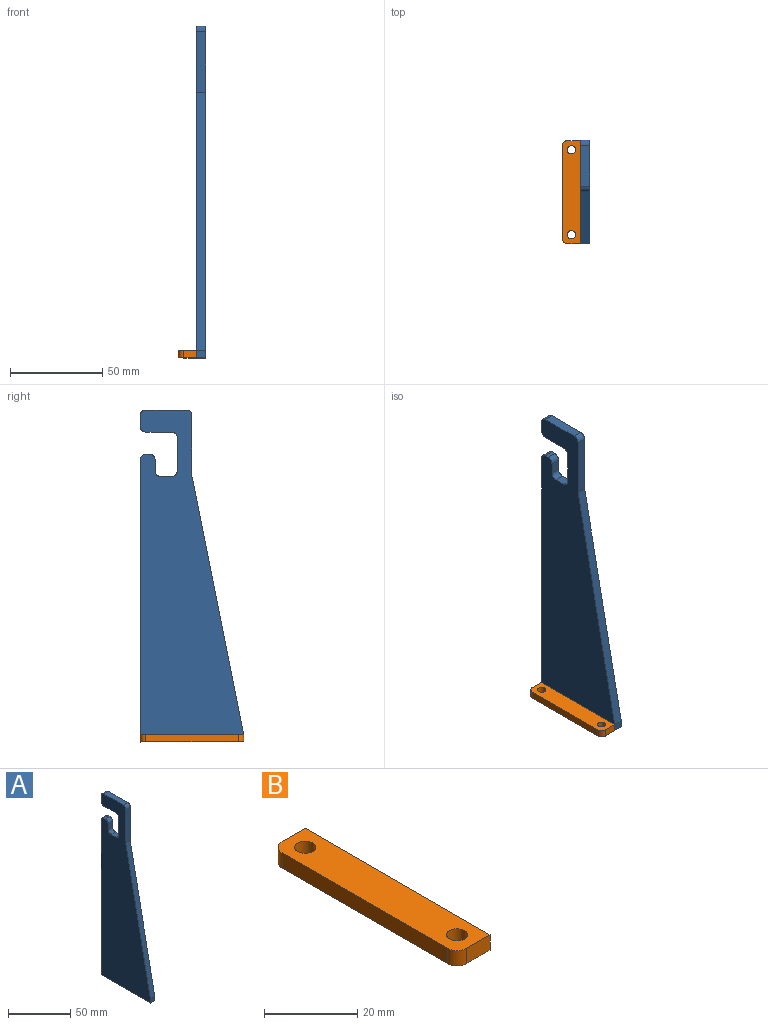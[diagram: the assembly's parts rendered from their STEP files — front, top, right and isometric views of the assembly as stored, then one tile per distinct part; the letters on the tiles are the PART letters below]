
ASSEMBLY  parts=2 mates=1
PART A: 22 faces, bbox 5x56x180 mm
  f0: plane 153x5mm, normal (0,1,0), area 765mm2, adj f3,f5,f6,f15
  f1: plane 5x4mm, normal (0,-1,0), area 20mm2, adj f3,f5,f6,f7
  f2: plane 22.01x5mm, normal (0,0,1), area 110.1mm2, adj f3,f5,f20,f21
  f3: plane 180x56.03mm, normal (1,0,0), area 6727.6mm2, adj f0,f1,f2,f4,f6,f7,f8,f9
  f4: plane 6x5mm, normal (0,1,0), area 30mm2, adj f3,f5,f16,f21
  f5: plane 180x56.03mm, normal (-1,0,0), area 6727.6mm2, adj f0,f1,f2,f4,f6,f7,f8,f9
  f6: plane 56.03x5mm, normal (0,0,-1), area 280.1mm2, adj f0,f1,f3,f5
  f7: plane 140x28.01mm, normal (0,-0.98,0.2), area 713.9mm2, adj f1,f3,f5,f8
  f8: plane 33x5mm, normal (0,-1,0), area 165mm2, adj f3,f5,f7,f20
  f9: plane 6x5mm, normal (0,-1,0), area 30mm2, adj f3,f5,f14,f19
  f10: plane 5x2mm, normal (0,0,1), area 10mm2, adj f3,f5,f14,f15
  f11: plane 14.01x5mm, normal (0,0,-1), area 70.1mm2, adj f3,f5,f16,f17
  f12: plane 18x5mm, normal (0,1,0), area 90mm2, adj f3,f5,f17,f18
  f13: plane 6.01x5mm, normal (0,0,1), area 30.1mm2, adj f3,f5,f18,f19
  f14: cylinder r=3mm len=5mm, axis (1,0,0), area 23.6mm2, adj f3,f5,f9,f10
  f15: cylinder r=3mm len=5mm, axis (-1,0,0), area 23.6mm2, adj f0,f3,f5,f10
  f16: cylinder r=3mm len=5mm, axis (-1,0,0), area 23.6mm2, adj f3,f4,f5,f11
  f17: cylinder r=3mm len=5mm, axis (-1,0,0), area 23.6mm2, adj f3,f5,f11,f12
  f18: cylinder r=3mm len=5mm, axis (-1,0,0), area 23.6mm2, adj f3,f5,f12,f13
  f19: cylinder r=3mm len=5mm, axis (-1,0,0), area 23.6mm2, adj f3,f5,f9,f13
  f20: cylinder r=3mm len=5mm, axis (-1,0,0), area 23.6mm2, adj f2,f3,f5,f8
  f21: cylinder r=3mm len=5mm, axis (1,0,0), area 23.6mm2, adj f2,f3,f4,f5
PART B: 10 faces, bbox 10x56x4 mm
  f0: plane 56.03x4mm, normal (1,0,0), area 224.1mm2, adj f1,f5,f6,f7
  f1: plane 7x4mm, normal (0,1,0), area 28mm2, adj f0,f6,f7,f8
  f2: plane 50.03x4mm, normal (-1,0,0), area 200.1mm2, adj f6,f7,f8,f9
  f3: cylinder r=2.25mm len=4.5mm, axis (0,0,-1), area 56.5mm2, adj f6,f7
  f4: cylinder r=2.25mm len=4.5mm, axis (0,0,-1), area 56.5mm2, adj f6,f7
  f5: plane 7x4mm, normal (0,-1,0), area 28mm2, adj f0,f6,f7,f9
  f6: plane 56.03x10mm, normal (0,0,1), area 524.6mm2, adj f0,f1,f2,f3,f4,f5,f8,f9
  f7: plane 56.03x10mm, normal (0,0,-1), area 524.6mm2, adj f0,f1,f2,f3,f4,f5,f8,f9
  f8: cylinder r=3mm len=4mm, axis (0,0,1), area 18.8mm2, adj f1,f2,f6,f7
  f9: cylinder r=3mm len=4mm, axis (0,0,-1), area 18.8mm2, adj f2,f5,f6,f7
PLACE A t=(-91.16,-48.64,-104.8)mm
PLACE B t=(-91.16,-48.64,-104.8)mm
MATE fastened B.f0 <-> A.f5  axis (1,0,0) through (-93.66,-48.64,-104.8)mm
